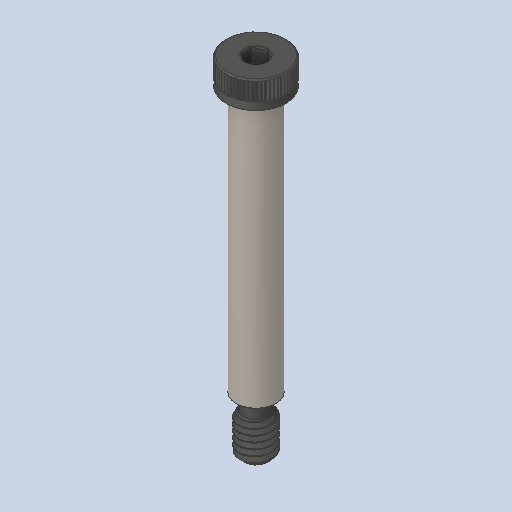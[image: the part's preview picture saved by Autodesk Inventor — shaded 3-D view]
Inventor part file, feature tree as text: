
AUTODESK INVENTOR PART (.ipt)
format: ipt  version: 2023 (Build 270158000, 158)  size: 424,960 bytes
history: native  units: in
note: dims shown in document units (in); Inventor stores cm internally (conversion verified against a paired STEP export)
features: chamfer x1
ambient origin geometry x8: Origin, YZ Plane, XZ Plane, XY Plane, X Axis, Y Axis, Z Axis, Center Point
bodies: Solid1 (feature_tree)
feature tree (1):
  chamfer  "Chamfer3"  [1 undecoded]
note: 1 required parameter value undecoded (feature->parameter linkage not recoverable at this tier; creation-order binding heuristic only, values carry confidence <= 0.55)
